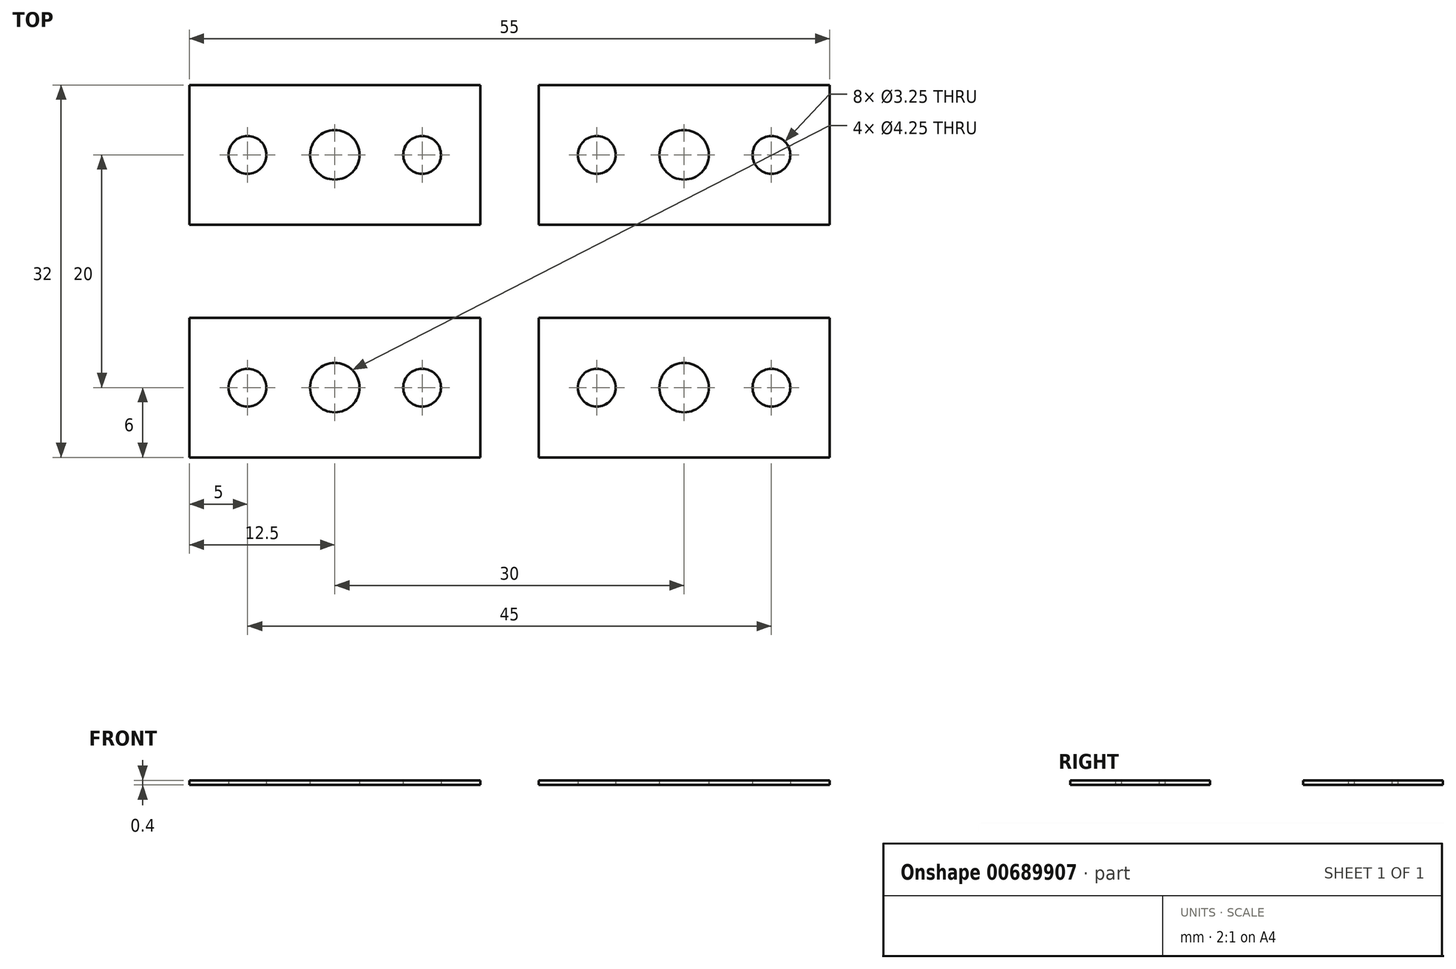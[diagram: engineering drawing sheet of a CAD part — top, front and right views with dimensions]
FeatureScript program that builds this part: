
annotation { "Feature Type Name" : "Feature", "Feature Type Description" : "" }
export const myFeature = defineFeature(function(context is Context, id is Id, definition is map)
    precondition{}
    {
        {
            var Q0;
            Q0=qCreatedBy(makeId("Top.planeOp"),FACE);
            var sketch = newSketch(context, id + "F0", { "sketchPlane" : qUnion([Q0])});
            skLineSegment(sketch, "E0.bottom", {"start": v(0, 0) * mm, "end": v(25, 0) * mm});
            skLineSegment(sketch, "E0.top", {"start": v(0, 12) * mm, "end": v(25, 12) * mm});
            skLineSegment(sketch, "E0.left", {"start": v(0, 0) * mm, "end": v(0, 12) * mm});
            skLineSegment(sketch, "E0.right", {"start": v(25, 0) * mm, "end": v(25, 12) * mm});
            skCircle(sketch, "E1", {"center": v(12.5, 6) * mm, "radius": 2.12 * mm});
            skCircle(sketch, "E2", {"center": v(5, 6) * mm, "radius": 1.63 * mm});
            skCircle(sketch, "E3", {"center": v(20, 6) * mm, "radius": 1.63 * mm});
            skLineSegment(sketch, "E4.0.1.0", {"start": v(25, 20) * mm, "end": v(25, 32) * mm});
            skLineSegment(sketch, "E4.0.1.1", {"start": v(0, 20) * mm, "end": v(25, 20) * mm});
            skCircle(sketch, "E4.0.1.2", {"center": v(12.5, 26) * mm, "radius": 2.12 * mm});
            skCircle(sketch, "E4.0.1.3", {"center": v(20, 26) * mm, "radius": 1.63 * mm});
            skCircle(sketch, "E4.0.1.4", {"center": v(5, 26) * mm, "radius": 1.63 * mm});
            skLineSegment(sketch, "E4.0.1.5", {"start": v(0, 20) * mm, "end": v(0, 32) * mm});
            skLineSegment(sketch, "E4.0.1.6", {"start": v(0, 32) * mm, "end": v(25, 32) * mm});
            skLineSegment(sketch, "E4.1.0.0", {"start": v(55, 0) * mm, "end": v(55, 12) * mm});
            skLineSegment(sketch, "E4.1.0.1", {"start": v(30, 0) * mm, "end": v(55, 0) * mm});
            skCircle(sketch, "E4.1.0.2", {"center": v(42.5, 6) * mm, "radius": 2.12 * mm});
            skCircle(sketch, "E4.1.0.3", {"center": v(50, 6) * mm, "radius": 1.63 * mm});
            skCircle(sketch, "E4.1.0.4", {"center": v(35, 6) * mm, "radius": 1.63 * mm});
            skLineSegment(sketch, "E4.1.0.5", {"start": v(30, 0) * mm, "end": v(30, 12) * mm});
            skLineSegment(sketch, "E4.1.0.6", {"start": v(30, 12) * mm, "end": v(55, 12) * mm});
            skLineSegment(sketch, "E4.1.1.0", {"start": v(55, 20) * mm, "end": v(55, 32) * mm});
            skLineSegment(sketch, "E4.1.1.1", {"start": v(30, 20) * mm, "end": v(55, 20) * mm});
            skCircle(sketch, "E4.1.1.2", {"center": v(42.5, 26) * mm, "radius": 2.12 * mm});
            skCircle(sketch, "E4.1.1.3", {"center": v(50, 26) * mm, "radius": 1.63 * mm});
            skCircle(sketch, "E4.1.1.4", {"center": v(35, 26) * mm, "radius": 1.63 * mm});
            skLineSegment(sketch, "E4.1.1.5", {"start": v(30, 20) * mm, "end": v(30, 32) * mm});
            skLineSegment(sketch, "E4.1.1.6", {"start": v(30, 32) * mm, "end": v(55, 32) * mm});
            skLineSegment(sketch, "E4.direction1", {"start": v(0, 0) * mm, "end": v(30, 0) * mm, "construction": true});
            skLineSegment(sketch, "E4.direction2", {"start": v(0, 0) * mm, "end": v(0, 20) * mm, "construction": true});
            skSolve(sketch);
        }
        {
            var Q0;
            Q0=makeQuery(id+"F0.imprint","IMPRINT",FACE,{"disambiguationData":[TD([[makeQuery(id+"F0.imprint","IMPRINT",EDGE,{"derivedFrom":sQuery(id+"F0.wireOp",EDGE,"E4.0.1.0")}),1.0]])]});
            var Q1;
            Q1=makeQuery(id+"F0.imprint","IMPRINT",FACE,{"disambiguationData":[TD([[makeQuery(id+"F0.imprint","IMPRINT",EDGE,{"derivedFrom":sQuery(id+"F0.wireOp",EDGE,"E4.1.1.0")}),1.0]])]});
            var Q2;
            Q2=makeQuery(id+"F0.imprint","IMPRINT",FACE,{"disambiguationData":[TD([[makeQuery(id+"F0.imprint","IMPRINT",EDGE,{"derivedFrom":sQuery(id+"F0.wireOp",EDGE,"E4.1.0.0")}),1.0]])]});
            var Q3;
            Q3=makeQuery(id+"F0.imprint","IMPRINT",FACE,{"disambiguationData":[TD([[makeQuery(id+"F0.imprint","IMPRINT",EDGE,{"derivedFrom":sQuery(id+"F0.wireOp",EDGE,"E0.bottom")}),1.0]])]});
            extrude(context, id + "F1", {"entities" : qUnion([Q0, Q1, Q2, Q3]), "depth" : 0.4 * mm, "offsetDistance" : 25 * mm});
        }
    });
